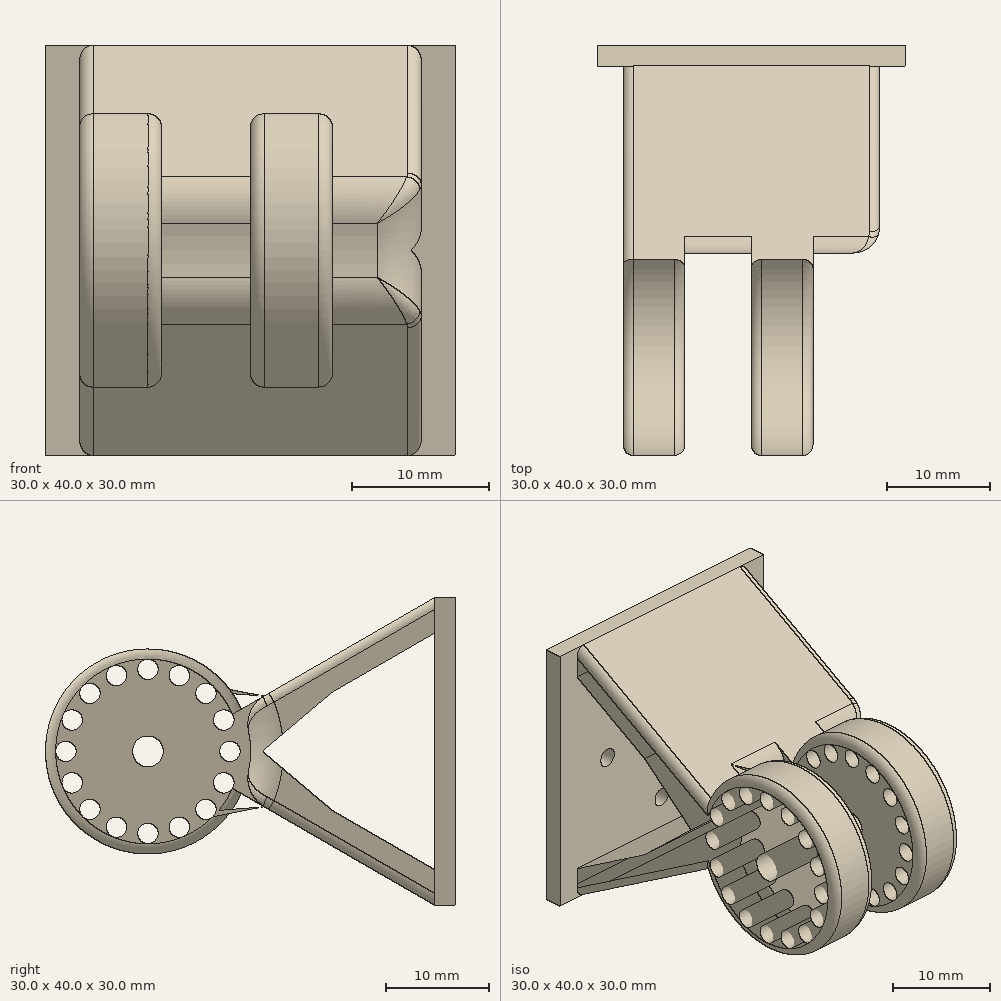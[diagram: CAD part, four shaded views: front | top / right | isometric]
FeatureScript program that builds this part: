
annotation { "Feature Type Name" : "Feature", "Feature Type Description" : "" }
export const myFeature = defineFeature(function(context is Context, id is Id, definition is map)
    precondition{}
    {
        {
            var Q0;
            Q0=qCreatedBy(makeId("Front.planeOp"),FACE);
            var sketch = newSketch(context, id + "F0", { "sketchPlane" : qUnion([Q0])});
            skLineSegment(sketch, "E0.bottom", {"start": v(-15, -15) * mm, "end": v(15, -15) * mm});
            skLineSegment(sketch, "E0.top", {"start": v(-15, 15) * mm, "end": v(15, 15) * mm});
            skLineSegment(sketch, "E0.left", {"start": v(-15, -15) * mm, "end": v(-15, 15) * mm});
            skLineSegment(sketch, "E0.right", {"start": v(15, -15) * mm, "end": v(15, 15) * mm});
            skCircle(sketch, "E1", {"center": v(-8, 0) * mm, "radius": 1 * mm});
            skCircle(sketch, "E2.1.0", {"center": v(0, -8) * mm, "radius": 1 * mm});
            skCircle(sketch, "E2.2.0", {"center": v(8, 0) * mm, "radius": 1 * mm});
            skCircle(sketch, "E2.3.0", {"center": v(0, 8) * mm, "radius": 1 * mm});
            skPoint(sketch, "E2.center", {"position": v(0, 0) * mm});
            skSolve(sketch);
        }
        {
            var Q0;
            Q0=makeQuery(id+"F0.imprint","IMPRINT",FACE,{"disambiguationData":[TD([[makeQuery(id+"F0.imprint","IMPRINT",EDGE,{"derivedFrom":sQuery(id+"F0.wireOp",EDGE,"E0.bottom")}),1.0]])]});
            extrude(context, id + "F1", {"entities" : qUnion([Q0]), "depth" : 2 * mm});
        }
        {
            var Q0;
            Q0=qCreatedBy(makeId("Right.planeOp"),FACE);
            var sketch = newSketch(context, id + "F2", { "sketchPlane" : qUnion([Q0])});
            skLineSegment(sketch, "E3", {"start": v(-2, 15) * mm, "end": v(-27.98, 0) * mm});
            skLineSegment(sketch, "E4", {"start": v(-27.98, 0) * mm, "end": v(-21.98, 0) * mm});
            skLineSegment(sketch, "E5", {"start": v(-21.98, 0) * mm, "end": v(-2, 11.54) * mm});
            skLineSegment(sketch, "E6", {"start": v(-2, 11.54) * mm, "end": v(-2, 15) * mm});
            skLineSegment(sketch, "E7.MirrorCS", {"start": v(-2, -11.54) * mm, "end": v(-2, -15) * mm});
            skLineSegment(sketch, "E8.MirrorCS", {"start": v(-2, -15) * mm, "end": v(-27.98, 0) * mm});
            skLineSegment(sketch, "E9.MirrorCS", {"start": v(-21.98, 0) * mm, "end": v(-2, -11.54) * mm});
            skSolve(sketch);
        }
        {
            var Q0;
            Q0=makeQuery(id+"F2.imprint","IMPRINT",FACE,{"disambiguationData":[TD([[makeQuery(id+"F2.imprint","IMPRINT",EDGE,{"derivedFrom":sQuery(id+"F2.wireOp",EDGE,"E3")}),1.0]])]});
            var Q1;
            Q1=makeQuery(id+"F2.imprint","IMPRINT",FACE,{"disambiguationData":[TD([[makeQuery(id+"F2.imprint","IMPRINT",EDGE,{"derivedFrom":sQuery(id+"F2.wireOp",EDGE,"E4")}),-1.0]])]});
            extrude(context, id + "F3", {"entities" : qUnion([Q0, Q1]), "operationType" : NewBodyOperationType.ADD, "endBound" : BoundingType.SYMMETRIC, "depth" : 25 * mm});
        }
        {
            var Q0;
            {var subQ0=sQuery(id+"F2.wireOp",EDGE,"E9.MirrorCS");var subQ1=sQuery(id+"F0.wireOp",EDGE,"E0.top");var subQ2=sQuery(id+"F0.wireOp",EDGE,"E0.bottom");var subQ4=sQuery(id+"F2.wireOp",EDGE,"E8.MirrorCS");var subQ6=sQuery(id+"F2.wireOp",EDGE,"E5");var subQ7=sQuery(id+"F2.wireOp",EDGE,"E3");var subQ8=makeQuery(id+"F3.opExtrude","CAP_FACE",FACE,{"disambiguationData":[OSD([subQ7,subQ6,sQuery(id+"F2.wireOp",EDGE,"E6"),sQuery(id+"F2.wireOp",EDGE,"E7.MirrorCS"),subQ4,subQ0])],"isStart":true});Q0=makeQuery(id+"F10.boolean.opBoolean","MERGE",FACE,{"derivedFrom":[makeQuery(id+"F9.boolean.opBoolean","SPLIT",FACE,{"disambiguationData":[TD([makeQuery(id+"F1.opExtrude","SWEPT_FACE",FACE,{"disambiguationData":[OSD([subQ1])]})])],"derivedFrom":subQ8}),makeQuery(id+"F9.boolean.opBoolean","SPLIT",FACE,{"disambiguationData":[TD([makeQuery(id+"F1.opExtrude","SWEPT_FACE",FACE,{"disambiguationData":[OSD([subQ2])]})])],"derivedFrom":subQ8}),makeQuery(id+"F10.opExtrude","CAP_FACE",FACE,{"disambiguationData":[OSD([sQuery(id+"F7.wireOp",EDGE,"E22"),sQuery(id+"F7.wireOp",EDGE,"E23"),sQuery(id+"F7.wireOp",EDGE,"E24"),sQuery(id+"F7.wireOp",EDGE,"E25.1.0"),sQuery(id+"F7.wireOp",EDGE,"E25.2.0"),sQuery(id+"F7.wireOp",EDGE,"E25.3.0"),sQuery(id+"F7.wireOp",EDGE,"E25.4.0"),sQuery(id+"F7.wireOp",EDGE,"E25.5.0"),sQuery(id+"F7.wireOp",EDGE,"E25.6.0"),sQuery(id+"F7.wireOp",EDGE,"E25.7.0"),sQuery(id+"F7.wireOp",EDGE,"E25.8.0"),sQuery(id+"F7.wireOp",EDGE,"E25.9.0"),sQuery(id+"F7.wireOp",EDGE,"E25.10.0"),sQuery(id+"F7.wireOp",EDGE,"E25.11.0"),sQuery(id+"F7.wireOp",EDGE,"E25.12.0"),sQuery(id+"F7.wireOp",EDGE,"E25.13.0"),sQuery(id+"F7.wireOp",EDGE,"E25.14.0"),sQuery(id+"F7.wireOp",EDGE,"E25.15.0")])],"isStart":true})]});}
            var sketch = newSketch(context, id + "F4", { "sketchPlane" : qUnion([Q0])});
            skLineSegment(sketch, "E10", {"start": v(12, 5.77) * mm, "end": v(18.82, 0) * mm});
            skLineSegment(sketch, "E11", {"start": v(18.82, 0) * mm, "end": v(12, -5.77) * mm});
            skLineSegment(sketch, "E12", {"start": v(12, -5.77) * mm, "end": v(12, 5.77) * mm});
            skLineSegment(sketch, "E13", {"start": v(12, 5.77) * mm, "end": v(23.02, -0.6) * mm});
            skLineSegment(sketch, "E14", {"start": v(23.02, -0.6) * mm, "end": v(22.96, 0.57) * mm});
            skLineSegment(sketch, "E15", {"start": v(22.96, 0.57) * mm, "end": v(12, -5.77) * mm});
            skSolve(sketch);
        }
        {
            var Q0;
            Q0=makeQuery(id+"F4.imprint","IMPRINT",FACE,{"disambiguationData":[TD([[makeQuery(id+"F4.imprint","IMPRINT",EDGE,{"derivedFrom":sQuery(id+"F4.wireOp",EDGE,"E10")}),1.0]])]});
            extrude(context, id + "F5", {"entities" : qUnion([Q0]), "operationType" : NewBodyOperationType.ADD, "oppositeDirection" : true, "depth" : 25 * mm});
        }
        {
            var Q0;
            Q0=qCreatedBy(makeId("Right.planeOp"),FACE);
            var sketch = newSketch(context, id + "F6", { "sketchPlane" : qUnion([Q0])});
            skCircle(sketch, "E16", {"center": v(-29.98, 0) * mm, "radius": 10 * mm});
            skCircle(sketch, "E17", {"center": v(-29.98, 0) * mm, "radius": 1.5 * mm});
            skPoint(sketch, "E18.center", {"position": v(0, 0) * mm});
            skCircle(sketch, "E19", {"center": v(-37.98, 0) * mm, "radius": 1 * mm});
            skCircle(sketch, "E20.1.0", {"center": v(-37.37, -3.06) * mm, "radius": 1 * mm});
            skCircle(sketch, "E20.2.0", {"center": v(-35.64, -5.66) * mm, "radius": 1 * mm});
            skCircle(sketch, "E21.1.3.0", {"center": v(-33.04, -7.4) * mm, "radius": 1 * mm});
            skCircle(sketch, "E21.1.4.0", {"center": v(-29.98, -8) * mm, "radius": 1 * mm});
            skCircle(sketch, "E21.1.5.0", {"center": v(-26.92, -7.4) * mm, "radius": 1 * mm});
            skCircle(sketch, "E21.1.6.0", {"center": v(-24.32, -5.66) * mm, "radius": 1 * mm});
            skCircle(sketch, "E21.1.7.0", {"center": v(-22.59, -3.06) * mm, "radius": 1 * mm});
            skCircle(sketch, "E21.1.8.0", {"center": v(-21.98, 0) * mm, "radius": 1 * mm});
            skCircle(sketch, "E21.1.9.0", {"center": v(-22.59, 3.06) * mm, "radius": 1 * mm});
            skCircle(sketch, "E21.1.10.0", {"center": v(-24.32, 5.66) * mm, "radius": 1 * mm});
            skCircle(sketch, "E21.1.11.0", {"center": v(-26.92, 7.4) * mm, "radius": 1 * mm});
            skCircle(sketch, "E21.1.12.0", {"center": v(-29.98, 8) * mm, "radius": 1 * mm});
            skCircle(sketch, "E21.1.13.0", {"center": v(-33.04, 7.4) * mm, "radius": 1 * mm});
            skCircle(sketch, "E21.1.14.0", {"center": v(-35.64, 5.66) * mm, "radius": 1 * mm});
            skCircle(sketch, "E21.1.15.0", {"center": v(-37.37, 3.06) * mm, "radius": 1 * mm});
            skSolve(sketch);
        }
        {
            var Q0;
            Q0=makeQuery(id+"F3.opExtrude","CAP_FACE",FACE,{"disambiguationData":[OSD([sQuery(id+"F2.wireOp",EDGE,"E3"),sQuery(id+"F2.wireOp",EDGE,"E5"),sQuery(id+"F2.wireOp",EDGE,"E6"),sQuery(id+"F2.wireOp",EDGE,"E7.MirrorCS"),sQuery(id+"F2.wireOp",EDGE,"E8.MirrorCS"),sQuery(id+"F2.wireOp",EDGE,"E9.MirrorCS")])],"isStart":true});
            var sketch = newSketch(context, id + "F7", { "sketchPlane" : qUnion([Q0])});
            skCircle(sketch, "E22", {"center": v(29.98, 0) * mm, "radius": 1.5 * mm});
            skCircle(sketch, "E23", {"center": v(29.98, 0) * mm, "radius": 10 * mm});
            skCircle(sketch, "E24", {"center": v(37.98, 0) * mm, "radius": 1 * mm});
            skCircle(sketch, "E25.1.0", {"center": v(37.37, 3.06) * mm, "radius": 1 * mm});
            skCircle(sketch, "E25.2.0", {"center": v(35.64, 5.66) * mm, "radius": 1 * mm});
            skCircle(sketch, "E25.3.0", {"center": v(33.04, 7.4) * mm, "radius": 1 * mm});
            skCircle(sketch, "E25.4.0", {"center": v(29.98, 8) * mm, "radius": 1 * mm});
            skCircle(sketch, "E25.5.0", {"center": v(26.92, 7.4) * mm, "radius": 1 * mm});
            skCircle(sketch, "E25.6.0", {"center": v(24.32, 5.66) * mm, "radius": 1 * mm});
            skCircle(sketch, "E25.7.0", {"center": v(22.59, 3.06) * mm, "radius": 1 * mm});
            skCircle(sketch, "E25.8.0", {"center": v(21.98, 0) * mm, "radius": 1 * mm});
            skCircle(sketch, "E25.9.0", {"center": v(22.59, -3.06) * mm, "radius": 1 * mm});
            skCircle(sketch, "E25.10.0", {"center": v(24.32, -5.66) * mm, "radius": 1 * mm});
            skCircle(sketch, "E25.11.0", {"center": v(26.92, -7.4) * mm, "radius": 1 * mm});
            skCircle(sketch, "E25.12.0", {"center": v(29.98, -8) * mm, "radius": 1 * mm});
            skCircle(sketch, "E25.13.0", {"center": v(33.04, -7.4) * mm, "radius": 1 * mm});
            skCircle(sketch, "E25.14.0", {"center": v(35.64, -5.66) * mm, "radius": 1 * mm});
            skCircle(sketch, "E25.15.0", {"center": v(37.37, -3.06) * mm, "radius": 1 * mm});
            skSolve(sketch);
        }
        {
            var Q0;
            Q0=makeQuery(id+"F3.opExtrude","CAP_FACE",FACE,{"disambiguationData":[OSD([sQuery(id+"F2.wireOp",EDGE,"E3"),sQuery(id+"F2.wireOp",EDGE,"E5"),sQuery(id+"F2.wireOp",EDGE,"E6"),sQuery(id+"F2.wireOp",EDGE,"E7.MirrorCS"),sQuery(id+"F2.wireOp",EDGE,"E8.MirrorCS"),sQuery(id+"F2.wireOp",EDGE,"E9.MirrorCS")])],"isStart":false});
            var sketch = newSketch(context, id + "F8", { "sketchPlane" : qUnion([Q0])});
            skCircle(sketch, "E26", {"center": v(-29.98, 0) * mm, "radius": 10 * mm});
            skSolve(sketch);
        }
        {
            var Q0;
            {var subQ0=sQuery(id+"F8.wireOp",EDGE,"E26");var subQ1=makeQuery(id+"F3.opExtrude","CAP_EDGE",EDGE,{"disambiguationData":[OSD([sQuery(id+"F2.wireOp",EDGE,"E3")])],"isStart":false});var subQ2=makeQuery(id+"F8.imprint","INTERSECT",VERTEX,{"derivedFrom":[subQ1,subQ0]});Q0=makeQuery(id+"F8.imprint","IMPRINT",FACE,{"disambiguationData":[TD([[makeQuery(id+"F8.imprint","IMPRINT",EDGE,{"disambiguationData":[TD([[subQ2,-1.0]])],"derivedFrom":subQ0}),1.0]])]});}
            var Q1;
            {var subQ3=sQuery(id+"F8.wireOp",EDGE,"E26");var subQ6=makeQuery(id+"F3.opExtrude","CAP_EDGE",EDGE,{"disambiguationData":[OSD([sQuery(id+"F2.wireOp",EDGE,"E3")])],"isStart":false});var subQ8=makeQuery(id+"F8.imprint","INTERSECT",VERTEX,{"derivedFrom":[subQ6,subQ3]});Q1=makeQuery(id+"F8.imprint","IMPRINT",FACE,{"disambiguationData":[TD([[makeQuery(id+"F8.imprint","IMPRINT",EDGE,{"disambiguationData":[TD([[subQ8,1.0]])],"derivedFrom":subQ3}),1.0]])]});}
            extrude(context, id + "F9", {"entities" : qUnion([Q0, Q1]), "operationType" : NewBodyOperationType.REMOVE, "oppositeDirection" : true, "depth" : 30 * mm});
        }
        {
            var Q0;
            Q0=makeQuery(id+"F7.imprint","IMPRINT",FACE,{"disambiguationData":[TD([[makeQuery(id+"F7.imprint","IMPRINT",EDGE,{"derivedFrom":sQuery(id+"F7.wireOp",EDGE,"E22")}),-1.0]])]});
            var Q1;
            Q1=makeQuery(id+"F6.imprint","IMPRINT",FACE,{"disambiguationData":[TD([[makeQuery(id+"F6.imprint","IMPRINT",EDGE,{"derivedFrom":sQuery(id+"F6.wireOp",EDGE,"E16")}),1.0]])]});
            var Q2;
            {var subQ5=sQuery(id+"F7.wireOp",EDGE,"E23");var subQ6=makeQuery(id+"F3.opExtrude","CAP_EDGE",EDGE,{"disambiguationData":[OSD([sQuery(id+"F2.wireOp",EDGE,"E5")])],"isStart":true});var subQ7=makeQuery(id+"F7.imprint","INTERSECT",VERTEX,{"derivedFrom":[subQ6,subQ5]});Q2=makeQuery(id+"F7.imprint","IMPRINT",FACE,{"disambiguationData":[TD([[makeQuery(id+"F7.imprint","IMPRINT",EDGE,{"disambiguationData":[TD([[subQ7,1.0]])],"derivedFrom":subQ5}),1.0]])]});}
            var Q3;
            {var subQ0=sQuery(id+"F7.wireOp",EDGE,"E23");var subQ1=makeQuery(id+"F3.opExtrude","CAP_EDGE",EDGE,{"disambiguationData":[OSD([sQuery(id+"F2.wireOp",EDGE,"E5")])],"isStart":true});var subQ2=makeQuery(id+"F7.imprint","INTERSECT",VERTEX,{"derivedFrom":[subQ1,subQ0]});Q3=makeQuery(id+"F7.imprint","IMPRINT",FACE,{"disambiguationData":[TD([[makeQuery(id+"F7.imprint","IMPRINT",EDGE,{"disambiguationData":[TD([[subQ2,-1.0]])],"derivedFrom":subQ0}),1.0]])]});}
            var Q4;
            {var subQ0=sQuery(id+"F7.wireOp",EDGE,"E25.8.0");var subQ1=makeQuery(id+"F3.opExtrude","CAP_EDGE",EDGE,{"disambiguationData":[OSD([sQuery(id+"F2.wireOp",EDGE,"E5")])],"isStart":true});var subQ2=makeQuery(id+"F7.imprint","INTERSECT",VERTEX,{"derivedFrom":[subQ1,subQ0]});Q4=makeQuery(id+"F7.imprint","IMPRINT",FACE,{"disambiguationData":[TD([[makeQuery(id+"F7.imprint","IMPRINT",EDGE,{"disambiguationData":[TD([[subQ2,1.0]])],"derivedFrom":subQ0}),-1.0]])]});}
            extrude(context, id + "F10", {"entities" : qUnion([Q0, Q1, Q2, Q3, Q4]), "operationType" : NewBodyOperationType.ADD, "oppositeDirection" : true, "depth" : 6 * mm});
        }
        {
            var Q0;
            {var subQ0=sQuery(id+"F7.wireOp",EDGE,"E23");Q0=makeQuery(id+"F10.boolean.opBoolean","SPLIT",EDGE,{"disambiguationData":[topologyDisambiguationEdgeConnected([makeQuery(id+"F10.opExtrude","SWEPT_FACE",FACE,{"disambiguationData":[OSD([subQ0])]})])],"derivedFrom":makeQuery(id+"F10.opExtrude","CAP_EDGE",EDGE,{"disambiguationData":[OSD([subQ0])],"isStart":false})});}
            var Q1;
            {var subQ0=sQuery(id+"F6.wireOp",EDGE,"E16");Q1=makeQuery(id+"F10.boolean.opBoolean","SPLIT",EDGE,{"disambiguationData":[topologyDisambiguationEdgeConnected([makeQuery(id+"F10.opExtrude","SWEPT_FACE",FACE,{"disambiguationData":[OSD([subQ0])]})])],"derivedFrom":makeQuery(id+"F10.opExtrude","CAP_EDGE",EDGE,{"disambiguationData":[OSD([subQ0])],"isStart":false})});}
            var Q2;
            {var subQ0=sQuery(id+"F6.wireOp",EDGE,"E16");Q2=makeQuery(id+"F10.boolean.opBoolean","SPLIT",EDGE,{"disambiguationData":[topologyDisambiguationEdgeConnected([makeQuery(id+"F10.opExtrude","SWEPT_FACE",FACE,{"disambiguationData":[OSD([subQ0])]})])],"derivedFrom":makeQuery(id+"F10.opExtrude","CAP_EDGE",EDGE,{"disambiguationData":[OSD([subQ0])],"isStart":true})});}
            var Q3;
            Q3=makeQuery(id+"F10.opExtrude","CAP_EDGE",EDGE,{"disambiguationData":[OSD([sQuery(id+"F7.wireOp",EDGE,"E23")])],"isStart":true});
            fillet(context, id + "F11", {"entities" : qUnion([Q0, Q1, Q2, Q3]), "radius" : 1 * mm, "tangentPropagation" : true, "allowEdgeOverflow" : false});
        }
        {
            var Q0;
            Q0=makeQuery(id+"F3.opExtrude","CAP_EDGE",EDGE,{"disambiguationData":[OSD([sQuery(id+"F2.wireOp",EDGE,"E8.MirrorCS")])],"isStart":true});
            var Q1;
            Q1=makeQuery(id+"F3.opExtrude","CAP_EDGE",EDGE,{"disambiguationData":[OSD([sQuery(id+"F2.wireOp",EDGE,"E8.MirrorCS")])],"isStart":false});
            var Q2;
            Q2=makeQuery(id+"F3.opExtrude","CAP_EDGE",EDGE,{"disambiguationData":[OSD([sQuery(id+"F2.wireOp",EDGE,"E3")])],"isStart":false});
            var Q3;
            Q3=makeQuery(id+"F3.opExtrude","CAP_EDGE",EDGE,{"disambiguationData":[OSD([sQuery(id+"F2.wireOp",EDGE,"E3")])],"isStart":true});
            fillet(context, id + "F12", {"entities" : qUnion([Q0, Q1, Q2, Q3]), "radius" : 1 * mm, "tangentPropagation" : true, "allowEdgeOverflow" : false});
        }
        {
            var Q0;
            {var subQ0=makeQuery(id+"F3.opExtrude","SWEPT_FACE",FACE,{"disambiguationData":[OSD([sQuery(id+"F2.wireOp",EDGE,"E3")])]});Q0=makeQuery(id+"F10.boolean.opBoolean","SPLIT",EDGE,{"disambiguationData":[topologyDisambiguationEdgeConnected([subQ0,makeQuery(id+"F10.opExtrude","SWEPT_FACE",FACE,{"disambiguationData":[OSD([sQuery(id+"F7.wireOp",EDGE,"E23")])]})])],"derivedFrom":makeQuery(id+"F9.boolean.opBoolean","INTERSECT",EDGE,{"derivedFrom":[subQ0,makeQuery(id+"F9.opExtrude","SWEPT_FACE",FACE,{"disambiguationData":[OSD([sQuery(id+"F8.wireOp",EDGE,"E26")])]})]})});}
            var Q1;
            {var subQ0=makeQuery(id+"F3.opExtrude","SWEPT_FACE",FACE,{"disambiguationData":[OSD([sQuery(id+"F2.wireOp",EDGE,"E3")])]});Q1=makeQuery(id+"F10.boolean.opBoolean","SPLIT",EDGE,{"disambiguationData":[topologyDisambiguationEdgeConnected([subQ0,makeQuery(id+"F10.opExtrude","SWEPT_FACE",FACE,{"disambiguationData":[OSD([sQuery(id+"F6.wireOp",EDGE,"E16")])]})])],"derivedFrom":makeQuery(id+"F9.boolean.opBoolean","INTERSECT",EDGE,{"derivedFrom":[subQ0,makeQuery(id+"F9.opExtrude","SWEPT_FACE",FACE,{"disambiguationData":[OSD([sQuery(id+"F8.wireOp",EDGE,"E26")])]})]})});}
            var Q2;
            {var subQ0=makeQuery(id+"F3.opExtrude","SWEPT_FACE",FACE,{"disambiguationData":[OSD([sQuery(id+"F2.wireOp",EDGE,"E8.MirrorCS")])]});Q2=makeQuery(id+"F10.boolean.opBoolean","SPLIT",EDGE,{"disambiguationData":[topologyDisambiguationEdgeConnected([subQ0,makeQuery(id+"F10.opExtrude","SWEPT_FACE",FACE,{"disambiguationData":[OSD([sQuery(id+"F6.wireOp",EDGE,"E16")])]})])],"derivedFrom":makeQuery(id+"F9.boolean.opBoolean","INTERSECT",EDGE,{"derivedFrom":[subQ0,makeQuery(id+"F9.opExtrude","SWEPT_FACE",FACE,{"disambiguationData":[OSD([sQuery(id+"F8.wireOp",EDGE,"E26")])]})]})});}
            var Q3;
            {var subQ0=makeQuery(id+"F3.opExtrude","SWEPT_FACE",FACE,{"disambiguationData":[OSD([sQuery(id+"F2.wireOp",EDGE,"E8.MirrorCS")])]});Q3=makeQuery(id+"F10.boolean.opBoolean","SPLIT",EDGE,{"disambiguationData":[topologyDisambiguationEdgeConnected([subQ0,makeQuery(id+"F10.opExtrude","SWEPT_FACE",FACE,{"disambiguationData":[OSD([sQuery(id+"F7.wireOp",EDGE,"E23")])]})])],"derivedFrom":makeQuery(id+"F9.boolean.opBoolean","INTERSECT",EDGE,{"derivedFrom":[subQ0,makeQuery(id+"F9.opExtrude","SWEPT_FACE",FACE,{"disambiguationData":[OSD([sQuery(id+"F8.wireOp",EDGE,"E26")])]})]})});}
            fillet(context, id + "F13", {"entities" : qUnion([Q0, Q1, Q2, Q3]), "radius" : 3.2 * mm, "tangentPropagation" : true, "allowEdgeOverflow" : false});
        }
    });
